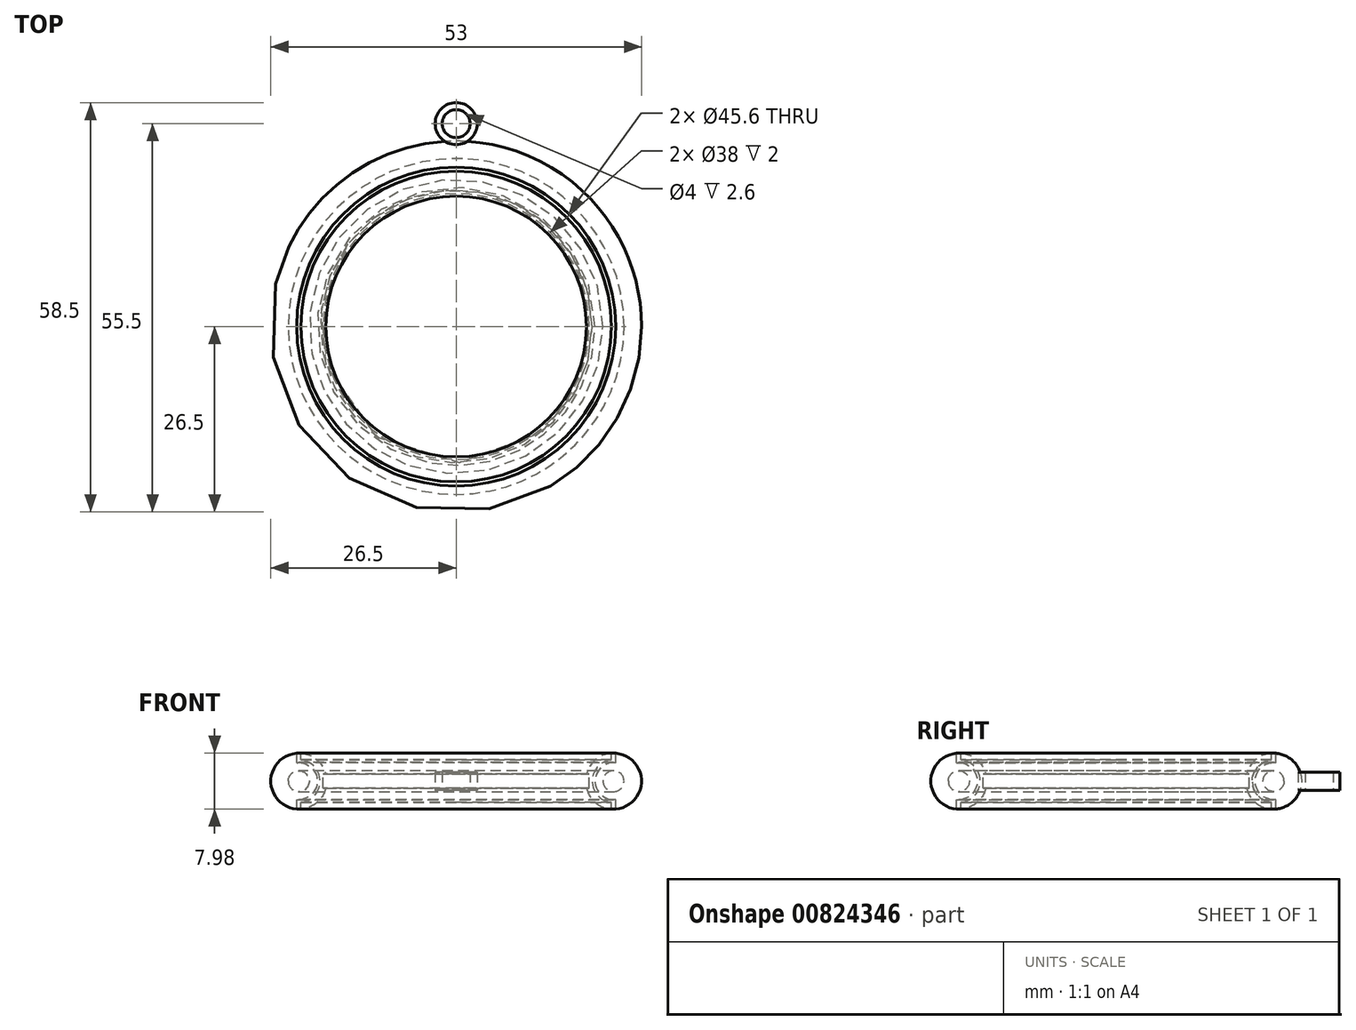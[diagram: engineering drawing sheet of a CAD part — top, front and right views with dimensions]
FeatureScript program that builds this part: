
annotation { "Feature Type Name" : "Feature", "Feature Type Description" : "" }
export const myFeature = defineFeature(function(context is Context, id is Id, definition is map)
    precondition{}
    {
        {
            var Q0;
            Q0=qCreatedBy(makeId("Top.planeOp"),FACE);
            var sketch = newSketch(context, id + "F0", { "sketchPlane" : qUnion([Q0])});
            skCircle(sketch, "E0", {"center": v(0, 0) * mm, "radius": 22.5 * mm});
            skSolve(sketch);
        }
        {
            var Q0;
            Q0=qCreatedBy(makeId("Right.planeOp"),FACE);
            var sketch = newSketch(context, id + "F1", { "sketchPlane" : qUnion([Q0])});
            skLineSegment(sketch, "E1", {"start": v(0, 0) * mm, "end": v(22.5, 0) * mm, "construction": true});
            skArc(sketch, "E2", {"start": v(22.2, 3.99) * mm, "mid": v(19.93, 3.07) * mm, "end": v(18.63, 1) * mm});
            skArc(sketch, "E3", {"start": v(22.2, 3.04) * mm, "mid": v(19.45, 0) * mm, "end": v(22.2, -3.04) * mm});
            skLineSegment(sketch, "E4", {"start": v(22.5, 0) * mm, "end": v(22.8, 0) * mm, "construction": true});
            skLineSegment(sketch, "E5", {"start": v(22.8, 2.63) * mm, "end": v(22.8, 3.99) * mm});
            skArc(sketch, "E6", {"start": v(22.8, 2.63) * mm, "mid": v(19.85, 0) * mm, "end": v(22.8, -2.63) * mm});
            skLineSegment(sketch, "E7.MirrorCS", {"start": v(22.8, -2.63) * mm, "end": v(22.8, -3.99) * mm});
            skLineSegment(sketch, "E8.top", {"start": v(19, 1) * mm, "end": v(18.63, 1) * mm});
            skLineSegment(sketch, "E8.left", {"start": v(19, -1) * mm, "end": v(19, 1) * mm});
            skPoint(sketch, "E8.middle", {"position": v(16.8, 0) * mm});
            skArc(sketch, "E9.trimOffspring", {"start": v(18.63, -1) * mm, "mid": v(19.93, -3.07) * mm, "end": v(22.2, -3.99) * mm});
            skLineSegment(sketch, "E10", {"start": v(19, -1) * mm, "end": v(18.63, -1) * mm});
            skArc(sketch, "E11.trimOffspring", {"start": v(22.8, -3.99) * mm, "mid": v(26.5, 0) * mm, "end": v(22.8, 3.99) * mm});
            skLineSegment(sketch, "E12", {"start": v(22.5, 0) * mm, "end": v(22.2, 0) * mm, "construction": true});
            skLineSegment(sketch, "E13", {"start": v(22.2, -3.04) * mm, "end": v(22.2, -3.99) * mm});
            skLineSegment(sketch, "E14.MirrorCS", {"start": v(22.2, 3.04) * mm, "end": v(22.2, 3.99) * mm});
            skCircle(sketch, "E15", {"center": v(22.5, 0) * mm, "radius": 1.5 * mm});
            skSolve(sketch);
        }
        {
            var Q0;
            Q0=makeQuery(id+"F1.imprint","IMPRINT",FACE,{"disambiguationData":[TD([[makeQuery(id+"F1.imprint","IMPRINT",EDGE,{"derivedFrom":sQuery(id+"F1.wireOp",EDGE,"E2")}),1.0]])]});
            var Q1;
            Q1=sQuery(id+"F0.wireOp",EDGE,"E0");
            sweep(context, id + "F2", {"profiles" : qUnion([Q0]), "path" : qUnion([Q1])});
        }
        {
            var Q0;
            Q0=qCreatedBy(makeId("Top.planeOp"),FACE);
            var sketch = newSketch(context, id + "F3", { "sketchPlane" : qUnion([Q0])});
            skLineSegment(sketch, "E16", {"start": v(0, 0) * mm, "end": v(0, 26) * mm, "construction": true});
            skLineSegment(sketch, "E17", {"start": v(0, 26) * mm, "end": v(0, 29) * mm, "construction": true});
            skCircle(sketch, "E18", {"center": v(0, 29) * mm, "radius": 2 * mm});
            skCircle(sketch, "E19", {"center": v(0, 29) * mm, "radius": 3 * mm});
            skSolve(sketch);
        }
        {
            var Q0;
            Q0=makeQuery(id+"F3.imprint","IMPRINT",FACE,{"disambiguationData":[TD([[makeQuery(id+"F3.imprint","IMPRINT",EDGE,{"derivedFrom":sQuery(id+"F3.wireOp",EDGE,"E18")}),-1.0]])]});
            extrude(context, id + "F4", {"entities" : qUnion([Q0]), "depth" : 1.3 * mm, "offsetDistance" : 25 * mm, "hasSecondDirection" : true, "secondDirectionOppositeDirection" : true, "secondDirectionDepth" : 1.3 * mm});
        }
        {
            var Q0;
            Q0=qCreatedBy(makeId("Right.planeOp"),FACE);
            var sketch = newSketch(context, id + "F5", { "sketchPlane" : qUnion([Q0])});
            skLineSegment(sketch, "E20", {"start": v(0, 0) * mm, "end": v(0, -25.62) * mm});
            skSolve(sketch);
        }
        {
            var Q0;
            Q0 = qSketchRegion(id + "F1", true);
            var Q1;
            Q1=sQuery(id+"F5.wireOp",EDGE,"E20");
            revolve(context, id + "F6", {"surfaceOperationType" : NewSurfaceOperationType.NEW, "entities" : qUnion([Q0]), "axis" : qUnion([Q1]), "revolveType" : RevolveType.FULL});
        }
    });
